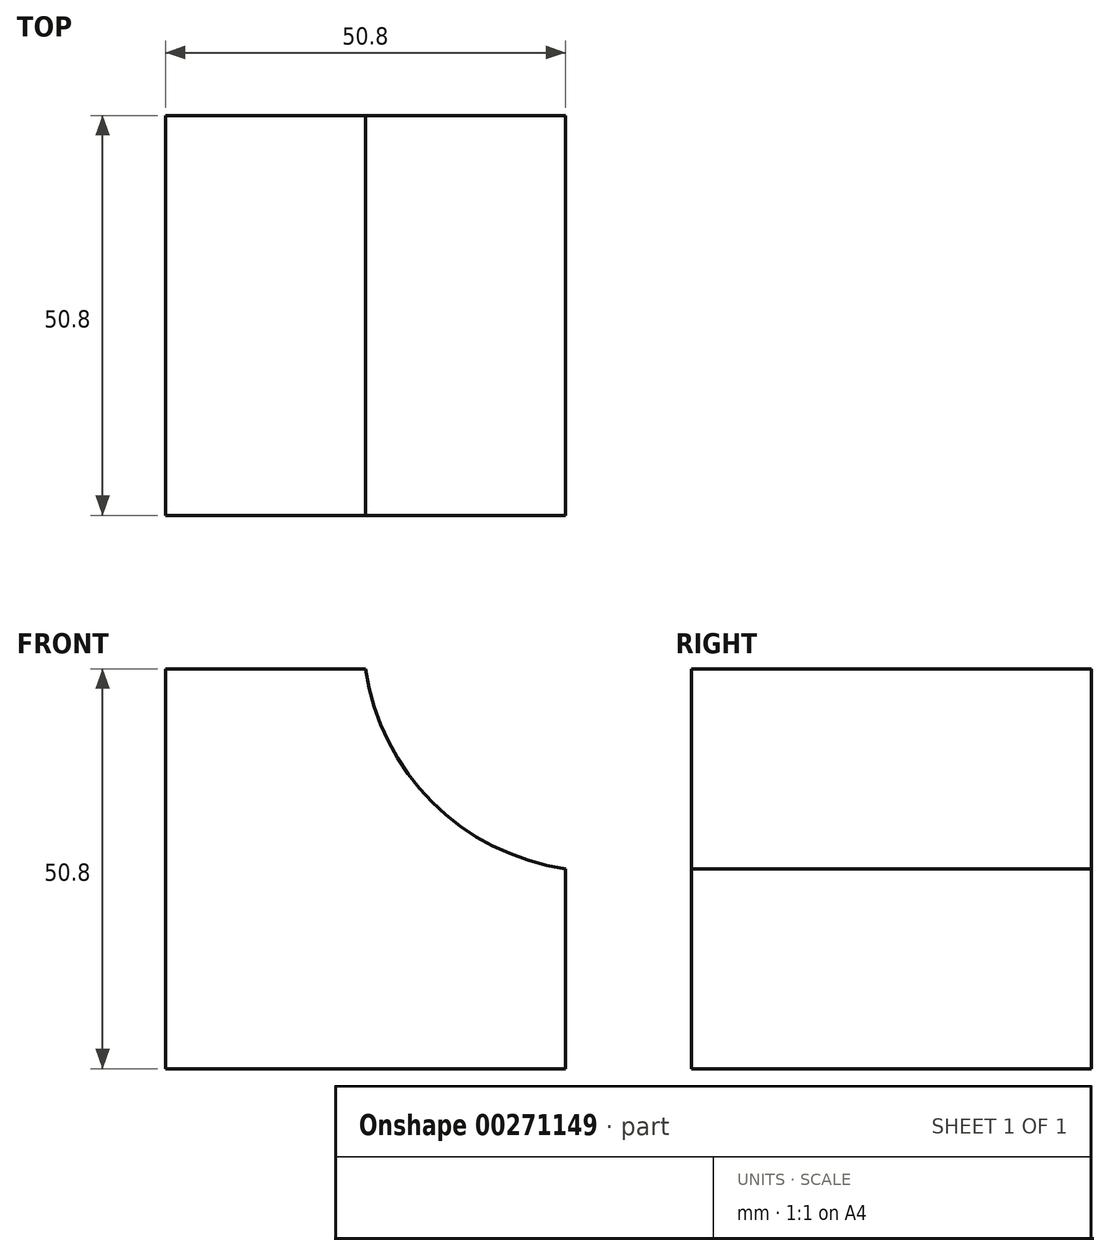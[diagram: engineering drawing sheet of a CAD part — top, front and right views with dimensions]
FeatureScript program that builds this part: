
annotation { "Feature Type Name" : "Feature", "Feature Type Description" : "" }
export const myFeature = defineFeature(function(context is Context, id is Id, definition is map)
    precondition{}
    {
        {
            var Q0;
            Q0=qCreatedBy(makeId("Front.planeOp"),FACE);
            var sketch = newSketch(context, id + "F0", { "sketchPlane" : qUnion([Q0])});
            skLineSegment(sketch, "E0", {"start": v(0, 0) * mm, "end": v(-50.8, 0) * mm});
            skLineSegment(sketch, "E1", {"start": v(-50.8, 0) * mm, "end": v(-50.8, 50.8) * mm});
            skLineSegment(sketch, "E2", {"start": v(-50.8, 50.8) * mm, "end": v(-25.4, 50.8) * mm});
            skLineSegment(sketch, "E3", {"start": v(0, 0) * mm, "end": v(0, 25.4) * mm});
            skArc(sketch, "E4", {"start": v(-25.4, 50.8) * mm, "mid": v(-16.94, 33.86) * mm, "end": v(0, 25.4) * mm});
            skSolve(sketch);
        }
        {
            var Q0;
            Q0 = qSketchRegion(id + "F0", true);
            extrude(context, id + "F1", {"entities" : qUnion([Q0]), "depth" : 50.8 * mm});
        }
    });
